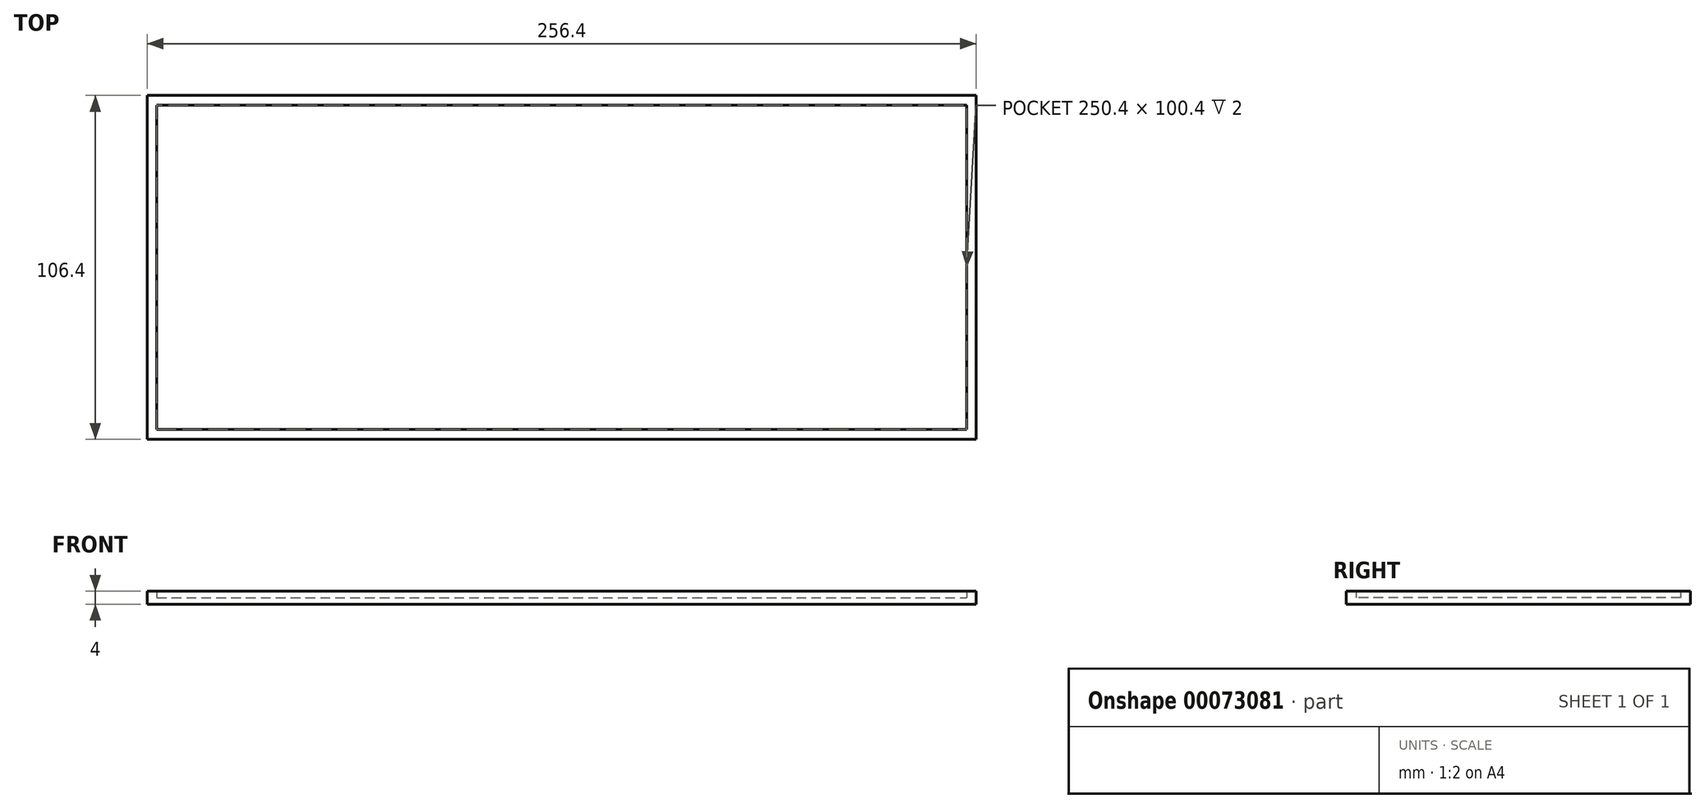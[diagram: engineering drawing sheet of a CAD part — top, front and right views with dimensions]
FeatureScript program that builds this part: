
annotation { "Feature Type Name" : "Feature", "Feature Type Description" : "" }
export const myFeature = defineFeature(function(context is Context, id is Id, definition is map)
    precondition{}
    {
        {
            var Q0;
            Q0=qCreatedBy(makeId("Top.planeOp"),FACE);
            var sketch = newSketch(context, id + "F0", { "sketchPlane" : qUnion([Q0])});
            skLineSegment(sketch, "E0.rect.bottom", {"start": v(-128.2, 53.2) * mm, "end": v(128.2, 53.2) * mm});
            skLineSegment(sketch, "E0.rect.top", {"start": v(-128.2, -53.2) * mm, "end": v(128.2, -53.2) * mm});
            skLineSegment(sketch, "E0.rect.left", {"start": v(-128.2, 53.2) * mm, "end": v(-128.2, -53.2) * mm});
            skLineSegment(sketch, "E0.rect.right", {"start": v(128.2, 53.2) * mm, "end": v(128.2, -53.2) * mm});
            skPoint(sketch, "E0.rect.middle", {"position": v(0, 0) * mm});
            skLineSegment(sketch, "E1.rect.bottom", {"start": v(-125.2, 50.2) * mm, "end": v(125.2, 50.2) * mm});
            skLineSegment(sketch, "E1.rect.left", {"start": v(-125.2, 50.2) * mm, "end": v(-125.2, -50.2) * mm});
            skLineSegment(sketch, "E1.rect.right", {"start": v(125.2, 50.2) * mm, "end": v(125.2, -50.2) * mm});
            skLineSegment(sketch, "E2", {"start": v(-125.2, -50.2) * mm, "end": v(125.2, -50.2) * mm});
            skSolve(sketch);
        }
        {
            var Q0;
            Q0=makeQuery(id+"F0.imprint","IMPRINT",FACE,{"disambiguationData":[TD([[makeQuery(id+"F0.imprint","IMPRINT",EDGE,{"derivedFrom":sQuery(id+"F0.wireOp",EDGE,"E1.rect.bottom")}),-1.0]])]});
            extrude(context, id + "F1", {"entities" : qUnion([Q0]), "depth" : 2 * mm});
        }
        {
            var Q0;
            Q0=makeQuery(id+"F0.imprint","IMPRINT",FACE,{"disambiguationData":[TD([[makeQuery(id+"F0.imprint","IMPRINT",EDGE,{"derivedFrom":sQuery(id+"F0.wireOp",EDGE,"E0.rect.bottom")}),-1.0]])]});
            extrude(context, id + "F2", {"entities" : qUnion([Q0]), "operationType" : NewBodyOperationType.ADD, "depth" : 4 * mm});
        }
    });
